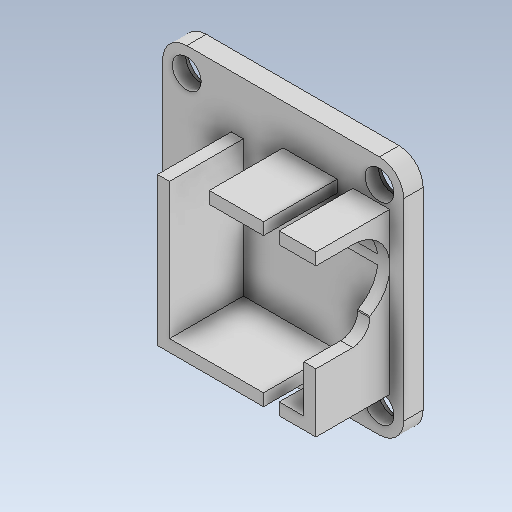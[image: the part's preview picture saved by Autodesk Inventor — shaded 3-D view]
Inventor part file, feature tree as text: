
AUTODESK INVENTOR PART (.ipt)
format: ipt  version: 2020 (Build 240168000, 168)  size: 222,720 bytes
history: native  units: mm
features: other x22, extrude x4, sketch x4
ambient origin geometry x8: Origin, YZ Plane, XZ Plane, XY Plane, X Axis, Y Axis, Z Axis, Center Point
bodies: Body1 (feature_tree)
feature tree (30):
  other  "Sólido1"
  extrude  "Extrusão1"  Depth=8.0mm
  extrude  "Extrusão2"  Depth=3.25mm TaperAngle=0.0deg
  extrude  "Extrusão3"  Depth=12.25mm TaperAngle=0.0deg
  extrude  "Extrusão4"  Depth=1.0mm
  sketch  "Esboço1"  dims[d0=8.0mm d1=8.0mm]
  other  "Referência1"
  other  "Referência2"
  other  "Referência3"
  other  "Referência4"
  sketch  "Esboço2"  dims[d2=8.0mm d3=3.25mm d4=0.0mm]
  other  "Referência5"
  other  "Referência6"
  other  "Referência7"
  sketch  "Esboço3"  dims[d6=12.25mm d7=0.0mm d8=12.25mm d9=0.0mm]
  sketch  "Esboço4"  dims[d10=1.0mm d11=0.0mm d12=8.0mm]
  other  "Referência8"
  other  "Referência9"
  other  "Referência10"
  other  "Referência11"
  other  "Referência12"
  other  "Referência13"
  other  "Referência14"
  other  "Referência15"
  other  "Referência16"
  other  "<userpath>\Desktop\rabo\3d\ela.iam"
  other  "ela.iam"
  other  "basesinha:1"
  other  "Component2_3_MIR:1"
  other  "microservoSG90:1"
